FCSTD DOCUMENT  (FreeCAD 1.0R39109 (Git))
Label: exhaust-plenum
License: All rights reserved
LicenseURL: http://en.wikipedia.org/wiki/All_rights_reserved
objects: Sketcher::SketchObject×3, PartDesign::Body×1
note: 7 computed .brp shape members not serialized (recipe doc carries the construction recipe); baked Part::Feature solids carry a one-line shape summary decoded from their .brp
EXTERNAL_REF file=enclosure-dims.FCStd obj=Spreadsheet

FEATURE [Sketcher::SketchObject] Sketch  label="round"
  ArcFitTolerance = 0
  FullyConstrained = true
  MakeInternals = false
  MapMode = 5
  Placement = pos=(0,0,0) rot=(0.57735,0.57735,0.57735;2.0944rad)
  sketch-geometry (1):
    g0: Circle CenterX=0 CenterY=-12.7 CenterZ=0 NormalX=0 NormalY=0 NormalZ=1 AngleXU=0 Radius=76.2
  constraints (3):
    c: PointOnObject(g0,g-2)
    c: Diameter(g0) = 152.4
    c: DistanceY(g0,g-1) = 12.7
FEATURE [Sketcher::SketchObject] Sketch001  label="rect"
  ArcFitTolerance = 0
  FullyConstrained = true
  MakeInternals = false
  Placement = pos=(0,0,203.2) rot=(0,0,1;0rad)
  expr: Constraints[7] = <<enclosure-dims>>#<<Spreadsheet>>.exhaust_w
  expr: Constraints[8] = <<enclosure-dims>>#<<Spreadsheet>>.exhaust_d
  sketch-geometry (4):
    g0: LineSegment StartX=307.975 StartY=-292.1 StartZ=0 EndX=358.775 EndY=-292.1 EndZ=0
    g1: LineSegment StartX=358.775 StartY=-292.1 StartZ=0 EndX=358.775 EndY=292.1 EndZ=0
    g2: LineSegment StartX=358.775 StartY=292.1 StartZ=0 EndX=307.975 EndY=292.1 EndZ=0
    g3: LineSegment StartX=307.975 StartY=292.1 StartZ=0 EndX=307.975 EndY=-292.1 EndZ=0
  constraints (11):
    c: Coincident(g0,g1)
    c: Coincident(g1,g2)
    c: Coincident(g2,g3)
    c: Coincident(g3,g0)
    c: Horizontal(g0)
    c: Horizontal(g2)
    c: Vertical(g3)
    c: DistanceX(g2,g2) = 50.8
    c: DistanceY(g1,g1) = 584.2
    c: DistanceX(g-1,g2) = 307.975
    c: Symmetric(g1,g0,g-1)
FEATURE [Sketcher::SketchObject] Sketch002  label="path"
  ArcFitTolerance = 0
  FullyConstrained = true
  MakeInternals = false
  Placement = pos=(0,0,0) rot=(1,0,0;1.5708rad)
  expr: Constraints[7] = (<<enclosure-dims>>#<<Spreadsheet>>.floor_w + <<enclosure-dims>>#<<Spreadsheet>>.exhaust_w) / 2
  sketch-geometry (3):
    g0: LineSegment StartX=0 StartY=0 StartZ=0 EndX=152.4 EndY=0 EndZ=0
    g1: LineSegment StartX=330.402 StartY=178.002 StartZ=0 EndX=330.402 EndY=203.2 EndZ=0
    g2: ArcOfCircle CenterX=152.4 CenterY=178.002 CenterZ=0 NormalX=0 NormalY=0 NormalZ=1 AngleXU=0 Radius=178.002 StartAngle=4.71239 EndAngle=6.28319
  constraints (8):
    c: Coincident(g-1,g0)
    c: Horizontal(g0)
    c: Vertical(g1)
    c: DistanceY(g1) = 203.2
    c: DistanceX(g0,g0) = 152.4
    c: Tangent(g2,g0) = -1.5708
    c: Tangent(g2,g1) = -1.5708
    c: DistanceX(g-1,g1) = 495.3
FEATURE [PartDesign::Body] Body
  AllowCompound = false
  Group = -> [Sketch,Sketch001,Sketch002]
  Origin = -> Origin
